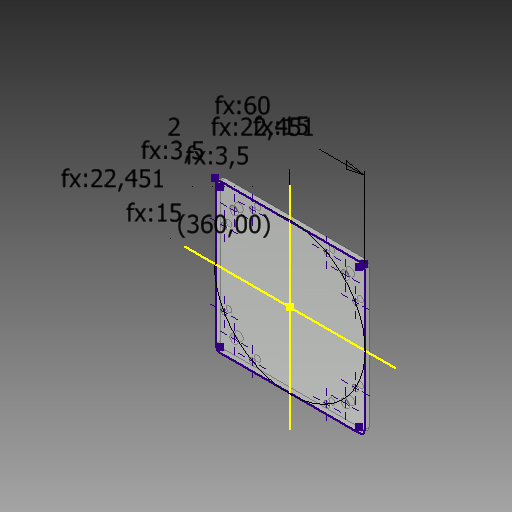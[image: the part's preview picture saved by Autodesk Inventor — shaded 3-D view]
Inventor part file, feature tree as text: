
AUTODESK INVENTOR PART (.ipt)
format: ipt  version: 2019 (Build 230136000, 136)  size: 144,896 bytes
history: native  units: mm
features: hole x2, other x1, sketch x1, extrude x1
ambient origin geometry x8: Origin, YZ Plane, XZ Plane, XY Plane, X Axis, Y Axis, Z Axis, Center Point
bodies: Solid1 (feature_tree)
feature tree (5):
  other  "<userpath>\OneDrive - Van Ierland\Documents\Inventor\FlightSim\Instrument.xlsx"
  sketch  "Sketch1"  dims[d0=60.0mm d1=2.0mm d2=22.45064mm d3=22.45064mm d4=15.0mm d5=15.0mm d6=3.5mm d7=3.5mm d8=40.0mm d10=360.0deg d12=2.0mm d13=0.0mm d14=3.4mm d15=6.0mm d16=6.3mm d17=2.0mm d18=90.0deg d19=8.0mm d20=20.594885mm d21=2.4mm d22=6.0mm d23=4.4mm d24=2.0mm d25=90.0deg d26=8.0mm d27=20.594885mm]
  extrude  "Extrusion1"  Depth=2.0mm
  hole  "Hole1"  [1 undecoded]
  hole  "Hole2"  [1 undecoded]
note: 2 required parameter values undecoded (feature->parameter linkage not recoverable at this tier; creation-order binding heuristic only, values carry confidence <= 0.55)
